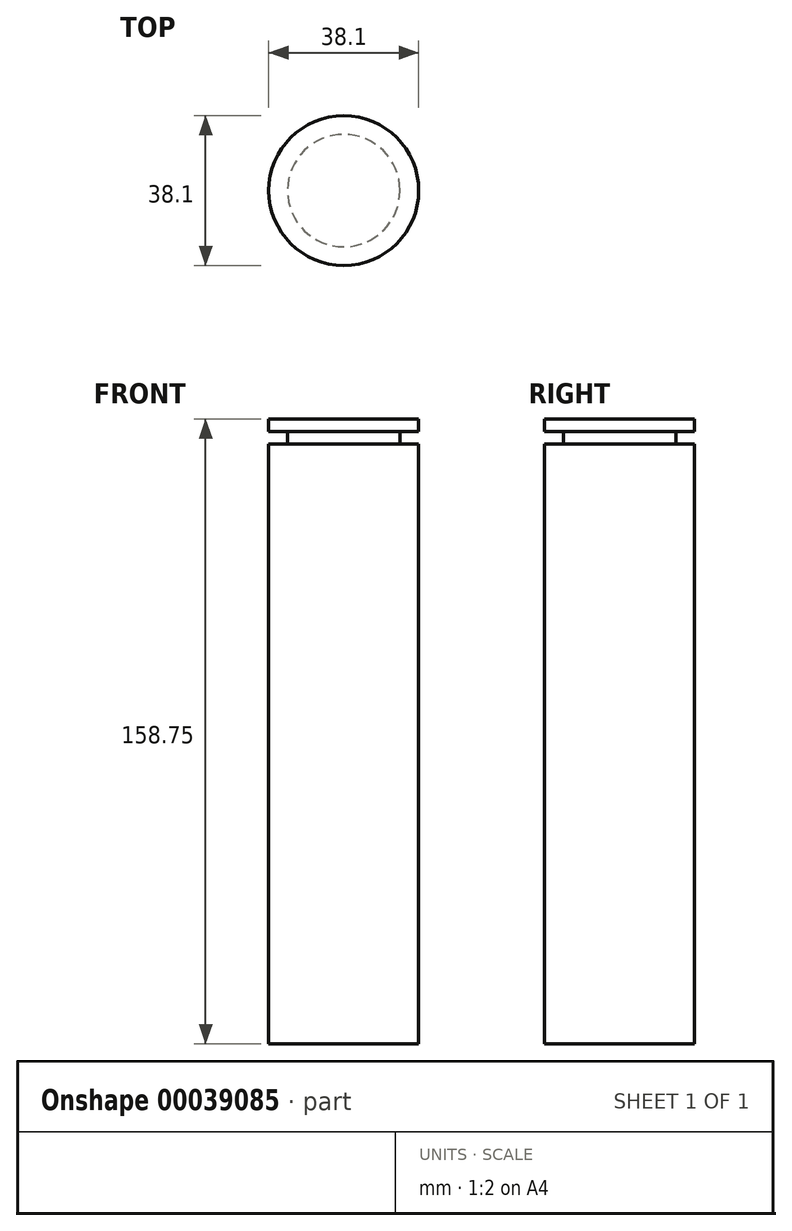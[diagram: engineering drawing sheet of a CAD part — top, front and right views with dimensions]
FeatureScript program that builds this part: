
annotation { "Feature Type Name" : "Feature", "Feature Type Description" : "" }
export const myFeature = defineFeature(function(context is Context, id is Id, definition is map)
    precondition{}
    {
        {
            var Q0;
            Q0=qCreatedBy(makeId("Top.planeOp"),FACE);
            var sketch = newSketch(context, id + "F0", { "sketchPlane" : qUnion([Q0])});
            skCircle(sketch, "E0", {"center": v(0, 0) * mm, "radius": 19.05 * mm});
            skSolve(sketch);
        }
        {
            var Q0;
            Q0 = qSketchRegion(id + "F0", true);
            extrude(context, id + "F1", {"entities" : qUnion([Q0]), "oppositeDirection" : true, "depth" : 152.4 * mm});
        }
        {
            var Q0;
            Q0=makeQuery(id+"F1.opExtrude","CAP_FACE",FACE,{"disambiguationData":[OSD([sQuery(id+"F0.wireOp",EDGE,"E0")])],"isStart":true});
            var sketch = newSketch(context, id + "F2", { "sketchPlane" : qUnion([Q0])});
            skCircle(sketch, "E1", {"center": v(0, 0) * mm, "radius": 8 * mm, "construction": true});
            skCircle(sketch, "E2", {"center": v(0, 0) * mm, "radius": 14.29 * mm});
            skSolve(sketch);
        }
        {
            var Q0;
            Q0=makeQuery(id+"F2.imprint","IMPRINT",FACE,{"disambiguationData":[TD([[makeQuery(id+"F2.imprint","IMPRINT",EDGE,{"derivedFrom":sQuery(id+"F2.wireOp",EDGE,"E2")}),1.0]])]});
            extrude(context, id + "F3", {"entities" : qUnion([Q0]), "operationType" : NewBodyOperationType.ADD, "depth" : 3.17 * mm});
        }
        {
            var Q0;
            Q0=makeQuery(id+"F3.opExtrude","CAP_FACE",FACE,{"disambiguationData":[OSD([sQuery(id+"F2.wireOp",EDGE,"E2")])],"isStart":false});
            var sketch = newSketch(context, id + "F4", { "sketchPlane" : qUnion([Q0])});
            skCircle(sketch, "E3", {"center": v(0, 0) * mm, "radius": 19.05 * mm});
            skSolve(sketch);
        }
        {
            var Q0;
            Q0 = qSketchRegion(id + "F4", true);
            extrude(context, id + "F5", {"entities" : qUnion([Q0]), "operationType" : NewBodyOperationType.ADD, "depth" : 3.17 * mm});
        }
    });
